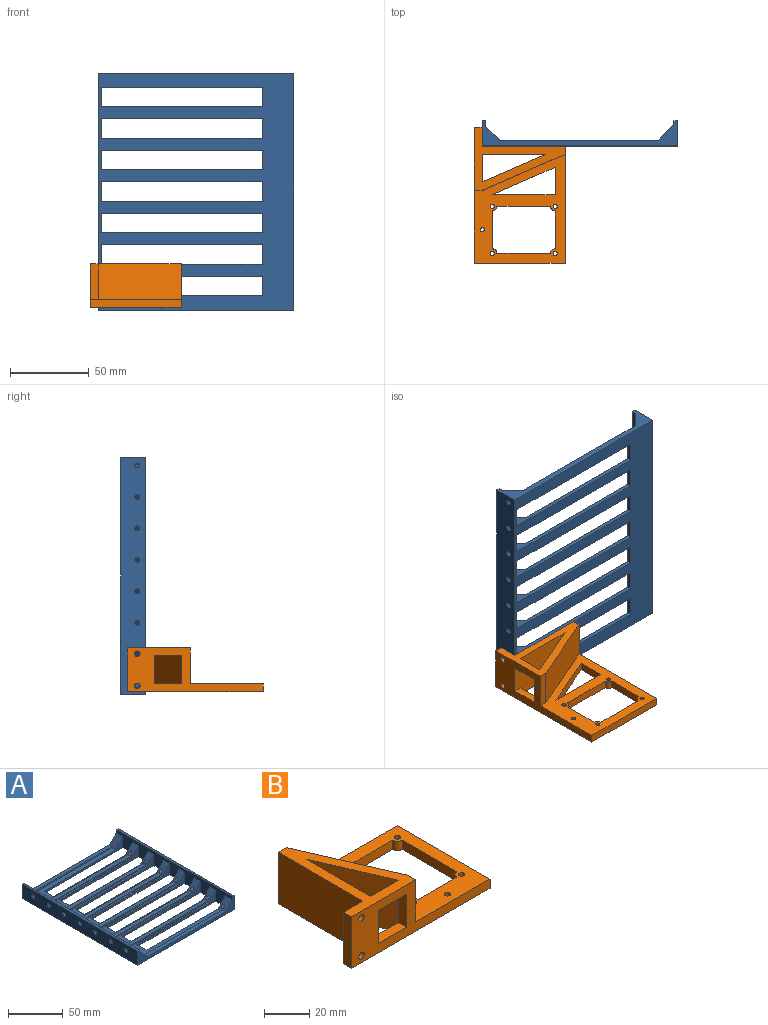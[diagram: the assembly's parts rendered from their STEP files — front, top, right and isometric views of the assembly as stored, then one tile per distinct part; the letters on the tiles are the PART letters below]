
ASSEMBLY  parts=2 mates=1
PART A: 90 faces, bbox 124.9x150.7x16.7 mm
  f0: plane 10.65x10.65mm, normal (-0.71,0,0.71), area 109.8mm2, adj f4,f6,f14,f28,f63,f64,f89
  f1: plane 10.65x10.65mm, normal (-0.71,0,0.71), area 102.7mm2, adj f4,f7,f27,f29,f77,f78,f82
  f2: plane 10.65x10.65mm, normal (-0.71,0,0.71), area 88.6mm2, adj f4,f8,f10,f21,f22,f71,f72,f73
  f3: plane 109.7x16mm, normal (0,0,1), area 605.2mm2, adj f12,f18,f19,f34,f48,f49,f59,f60
  f4: plane 150x16mm, normal (-1,0,0), area 1625mm2, adj f0,f1,f2,f9,f11,f14,f15,f16
  f5: plane 109.7x16mm, normal (0,0,1), area 605.2mm2, adj f12,f16,f17,f35,f47,f48,f57,f76
  f6: plane 109.7x19.25mm, normal (0,0,1), area 961.7mm2, adj f0,f12,f14,f15,f36,f47,f64,f74
  f7: plane 109.7x18.75mm, normal (0,0,1), area 906.9mm2, adj f1,f9,f12,f27,f30,f45,f67,f77
  f8: plane 109.7x16mm, normal (0,0,1), area 605.2mm2, adj f2,f12,f20,f21,f33,f49,f62,f71
  f9: plane 102x12.4mm, normal (0,1,0), area 294.8mm2, adj f4,f7,f11,f30,f45
  f10: plane 109.7x16mm, normal (0,0,1), area 605.2mm2, adj f2,f12,f22,f23,f32,f46,f68,f73
  f11: plane 150x124.2mm, normal (0,0,-1), area 9705mm2, adj f4,f9,f13,f14,f15,f16,f17,f18
  f12: plane 150x13.6mm, normal (1,0,0), area 1589.2mm2, adj f3,f5,f6,f7,f8,f10,f28,f29
  f13: plane 150x16mm, normal (-1,0,0), area 2307.6mm2, adj f11,f28,f29,f50,f51,f52,f53,f54
  f14: plane 102x12.4mm, normal (0,1,0), area 294.8mm2, adj f0,f4,f6,f11,f36
  f15: plane 102x12.4mm, normal (0,-1,0), area 294.8mm2, adj f4,f6,f11,f36,f47
  f16: plane 102x12.4mm, normal (0,1,0), area 294.8mm2, adj f4,f5,f11,f35,f47
  f17: plane 102x12.4mm, normal (0,-1,0), area 294.8mm2, adj f4,f5,f11,f35,f48
  f18: plane 102x12.4mm, normal (0,1,0), area 294.8mm2, adj f3,f4,f11,f34,f48
  f19: plane 102x12.4mm, normal (0,-1,0), area 294.8mm2, adj f3,f4,f11,f34,f49
  f20: plane 102x12.4mm, normal (0,1,0), area 294.8mm2, adj f4,f8,f11,f33,f49
  f21: plane 102x12.4mm, normal (0,-1,0), area 294.8mm2, adj f2,f4,f8,f11,f33
  f22: plane 102x12.4mm, normal (0,1,0), area 294.8mm2, adj f2,f4,f10,f11,f32
  f23: plane 102x12.4mm, normal (0,-1,0), area 294.8mm2, adj f4,f10,f11,f32,f46
  f24: plane 102x12.4mm, normal (0,1,0), area 294.8mm2, adj f4,f11,f31,f46,f79
  f25: plane 102x12.4mm, normal (0,-1,0), area 294.8mm2, adj f4,f11,f31,f45,f79
  f26: plane 150x16mm, normal (1,0,0), area 2339.6mm2, adj f11,f28,f29,f81,f82,f83,f84,f85
  f27: plane 102x12.4mm, normal (0,-1,0), area 294.8mm2, adj f1,f4,f7,f11,f30
  f28: plane 124.2x16mm, normal (0,-1,0), area 591.6mm2, adj f0,f4,f11,f12,f13,f26,f37,f63
  f29: plane 124.2x16mm, normal (0,1,0), area 591.6mm2, adj f1,f4,f11,f12,f13,f26,f43,f78
  f30: plane 12.5x2.4mm, normal (1,0,0), area 30mm2, adj f7,f9,f11,f27
  f31: plane 12.5x2.4mm, normal (1,0,0), area 30mm2, adj f11,f24,f25,f79
  f32: plane 12.5x2.4mm, normal (1,0,0), area 30mm2, adj f10,f11,f22,f23
  f33: plane 12.5x2.4mm, normal (1,0,0), area 30mm2, adj f8,f11,f20,f21
  f34: plane 12.5x2.4mm, normal (1,0,0), area 30mm2, adj f3,f11,f18,f19
  f35: plane 12.5x2.4mm, normal (1,0,0), area 30mm2, adj f5,f11,f16,f17
  f36: plane 12.5x2.4mm, normal (1,0,0), area 30mm2, adj f6,f11,f14,f15
  f37: plane 10x10mm, normal (0.71,0,0.71), area 56.6mm2, adj f12,f28,f63,f64
  f38: plane 10x10mm, normal (0.71,0,0.71), area 56.6mm2, adj f12,f74,f75,f76
  f39: plane 10x10mm, normal (0.71,0,0.71), area 56.6mm2, adj f12,f57,f58,f59
  f40: plane 10x10mm, normal (0.71,0,0.71), area 56.6mm2, adj f12,f60,f61,f62
  f41: plane 10x10mm, normal (0.71,0,0.71), area 56.6mm2, adj f12,f71,f72,f73
  f42: plane 10x10mm, normal (0.71,0,0.71), area 56.6mm2, adj f12,f68,f69,f70
  f43: plane 10x10mm, normal (0.71,0,0.71), area 56.6mm2, adj f12,f29,f77,f78
  f44: plane 10x10mm, normal (0.71,0,0.71), area 56.6mm2, adj f12,f65,f66,f67
  f45: plane 10.65x10.65mm, normal (-0.71,0,0.71), area 88.6mm2, adj f4,f7,f9,f25,f65,f66,f67,f79
  f46: plane 10.65x10.65mm, normal (-0.71,0,0.71), area 88.6mm2, adj f4,f10,f23,f24,f68,f69,f70,f79
  f47: plane 10.65x10.65mm, normal (-0.71,0,0.71), area 88.6mm2, adj f4,f5,f6,f15,f16,f74,f75,f76
  f48: plane 10.65x10.65mm, normal (-0.71,0,0.71), area 88.6mm2, adj f3,f4,f5,f17,f18,f57,f58,f59
  f49: plane 10.65x10.65mm, normal (-0.71,0,0.71), area 88.6mm2, adj f3,f4,f8,f19,f20,f60,f61,f62
  f50: cylinder r=2.05mm len=4.1mm, axis (-1,0,0), area 30.9mm2, adj f12,f13
  f51: cylinder r=2.05mm len=4.1mm, axis (-1,0,0), area 30.9mm2, adj f12,f13
  f52: cylinder r=2.05mm len=4.1mm, axis (-1,0,0), area 30.9mm2, adj f12,f13
  f53: cylinder r=2.05mm len=4.1mm, axis (-1,0,0), area 30.9mm2, adj f12,f13
  f54: cylinder r=2.05mm len=4.1mm, axis (-1,0,0), area 30.9mm2, adj f12,f13
  f55: cylinder r=2.05mm len=4.1mm, axis (-1,0,0), area 30.9mm2, adj f12,f13
  f56: cylinder r=2.05mm len=4.1mm, axis (-1,0,0), area 30.9mm2, adj f12,f13
  f57: plane 110.9x11.2mm, normal (0,-1,0), area 182.4mm2, adj f5,f12,f39,f48,f58
  f58: plane 100.9x4mm, normal (0,0,1), area 403.6mm2, adj f39,f48,f57,f59
  f59: plane 110.9x11.2mm, normal (0,1,0), area 182.4mm2, adj f3,f12,f39,f48,f58
  f60: plane 110.9x11.2mm, normal (0,-1,0), area 182.4mm2, adj f3,f12,f40,f49,f61
  f61: plane 100.9x4mm, normal (0,0,1), area 403.6mm2, adj f40,f49,f60,f62
  f62: plane 110.9x11.2mm, normal (0,1,0), area 182.4mm2, adj f8,f12,f40,f49,f61
  f63: plane 100.9x4mm, normal (0,0,1), area 403.6mm2, adj f0,f28,f37,f64
  f64: plane 110.9x11.2mm, normal (0,1,0), area 182.4mm2, adj f0,f6,f12,f37,f63
  f65: plane 110.9x11.2mm, normal (0,-1,0), area 182.4mm2, adj f12,f44,f45,f66,f79
  f66: plane 100.9x4mm, normal (0,0,1), area 403.6mm2, adj f44,f45,f65,f67
  f67: plane 110.9x11.2mm, normal (0,1,0), area 182.4mm2, adj f7,f12,f44,f45,f66
  f68: plane 110.9x11.2mm, normal (0,-1,0), area 182.4mm2, adj f10,f12,f42,f46,f69
  f69: plane 100.9x4mm, normal (0,0,1), area 403.6mm2, adj f42,f46,f68,f70
  f70: plane 110.9x11.2mm, normal (0,1,0), area 182.4mm2, adj f12,f42,f46,f69,f79
  f71: plane 110.9x11.2mm, normal (0,-1,0), area 182.4mm2, adj f2,f8,f12,f41,f72
  f72: plane 100.9x4mm, normal (0,0,1), area 403.6mm2, adj f2,f41,f71,f73
  f73: plane 110.9x11.2mm, normal (0,1,0), area 182.4mm2, adj f2,f10,f12,f41,f72
  f74: plane 110.9x11.2mm, normal (0,-1,0), area 182.4mm2, adj f6,f12,f38,f47,f75
  f75: plane 100.9x4mm, normal (0,0,1), area 403.6mm2, adj f38,f47,f74,f76
  f76: plane 110.9x11.2mm, normal (0,1,0), area 182.4mm2, adj f5,f12,f38,f47,f75
  f77: plane 110.9x11.2mm, normal (0,-1,0), area 182.4mm2, adj f1,f7,f12,f43,f78
  f78: plane 100.9x4mm, normal (0,0,1), area 403.6mm2, adj f1,f29,f43,f77
  f79: plane 109.7x16mm, normal (0,0,1), area 605.2mm2, adj f12,f24,f25,f31,f45,f46,f65,f70
  f80: plane 150x2.4mm, normal (0,0,1), area 360mm2, adj f12,f13,f28,f29
  f81: plane 150x2.1mm, normal (0,0,1), area 315mm2, adj f4,f26,f28,f29
  f82: cylinder r=1.55mm len=10.55mm, axis (1,0,0), area 87.1mm2, adj f1,f26
  f83: cylinder r=1.55mm len=10.55mm, axis (1,0,0), area 87.1mm2, adj f26,f45
  f84: cylinder r=1.55mm len=10.55mm, axis (1,0,0), area 87.1mm2, adj f26,f46
  f85: cylinder r=1.55mm len=10.55mm, axis (1,0,0), area 87.1mm2, adj f2,f26
  f86: cylinder r=1.55mm len=10.55mm, axis (1,0,0), area 87.1mm2, adj f26,f49
  f87: cylinder r=1.55mm len=10.55mm, axis (1,0,0), area 87.1mm2, adj f26,f48
  f88: cylinder r=1.55mm len=10.55mm, axis (1,0,0), area 87.1mm2, adj f26,f47
  f89: cylinder r=1.55mm len=10.55mm, axis (1,0,0), area 87.1mm2, adj f0,f26
PART B: 36 faces, bbox 86.4x57.7x27.8 mm
  f0: plane 17.5x5mm, normal (0,1,0), area 87.5mm2, adj f5,f6,f20,f33
  f1: plane 86.35x27.77mm, normal (0,-1,0), area 1012.4mm2, adj f2,f3,f5,f6,f7,f8,f9,f10
  f2: plane 86.35x57.7mm, normal (0,0,-1), area 2447.1mm2, adj f1,f4,f5,f7,f11,f12,f13,f14
  f3: plane 69.3x57.7mm, normal (0,0,1), area 1730.4mm2, adj f1,f10,f13,f14,f15,f16,f17,f18
  f4: plane 17.5x5mm, normal (0,1,0), area 87.5mm2, adj f2,f5,f20,f35
  f5: plane 45.18x27.77mm, normal (1,0,0), area 1204.6mm2, adj f0,f1,f2,f4,f6,f20,f33,f35
  f6: plane 57.7x40mm, normal (0,0,1), area 716.8mm2, adj f0,f1,f5,f7,f10,f11,f12,f13
  f7: plane 27.77x5mm, normal (-1,0,0), area 138.8mm2, adj f1,f2,f6,f11
  f8: cylinder r=1.75mm len=5mm, axis (0,-1,0), area 55mm2, adj f1,f11
  f9: cylinder r=1.75mm len=5mm, axis (0,-1,0), area 55mm2, adj f1,f11
  f10: plane 22.77x5mm, normal (1,0,0), area 113.8mm2, adj f1,f3,f6,f19
  f11: plane 27.77x12.05mm, normal (0,1,0), area 315.4mm2, adj f2,f6,f7,f8,f9,f12
  f12: plane 52.7x27.77mm, normal (-1,0,0), area 1463.5mm2, adj f2,f6,f11,f13
  f13: plane 74.3x27.77mm, normal (0,1,0), area 485.3mm2, adj f2,f3,f6,f12,f14,f19
  f14: plane 57.7x5mm, normal (1,0,0), area 288.5mm2, adj f1,f2,f3,f13
  f15: cylinder r=1.35mm len=5mm, axis (0,0,-1), area 42.4mm2, adj f2,f3
  f16: cylinder r=1.35mm len=5mm, axis (0,0,-1), area 42.4mm2, adj f2,f3
  f17: cylinder r=1.35mm len=5mm, axis (0,0,-1), area 42.4mm2, adj f2,f3
  f18: cylinder r=1.35mm len=5mm, axis (0,0,-1), area 42.4mm2, adj f2,f3
  f19: plane 52.7x22.95mm, normal (0.92,0.4,0), area 1308.8mm2, adj f3,f6,f10,f13
  f20: plane 40.18x27.77mm, normal (-0.92,-0.4,0), area 1216.9mm2, adj f0,f2,f4,f5,f6,f34
  f21: plane 40x5mm, normal (-1,0,0), area 200mm2, adj f2,f3,f22,f23
  f22: plane 17.42x5mm, normal (0,-1,0), area 87.1mm2, adj f2,f3,f21,f23
  f23: plane 40x17.42mm, normal (0.92,0.4,0), area 218.1mm2, adj f2,f3,f21,f22
  f24: plane 24x5mm, normal (0,1,0), area 120mm2, adj f2,f3,f28,f29
  f25: plane 34x5mm, normal (-1,0,0), area 170mm2, adj f2,f3,f29,f30
  f26: plane 24x5mm, normal (0,-1,0), area 120mm2, adj f2,f3,f30,f31
  f27: plane 34x5mm, normal (1,0,0), area 170mm2, adj f2,f3,f28,f31
  f28: cylinder r=3mm len=5mm, axis (0,0,1), area 23.6mm2, adj f2,f3,f24,f27
  f29: cylinder r=3mm len=5mm, axis (0,0,1), area 23.6mm2, adj f2,f3,f24,f25
  f30: cylinder r=3mm len=5mm, axis (0,0,1), area 23.6mm2, adj f2,f3,f25,f26
  f31: cylinder r=3mm len=5mm, axis (0,0,1), area 23.6mm2, adj f2,f3,f26,f27
  f32: cylinder r=1.35mm len=5mm, axis (0,0,1), area 42.4mm2, adj f2,f3
  f33: plane 17.5x5mm, normal (0,0,-1), area 87.5mm2, adj f0,f1,f5,f34
  f34: plane 17.77x5mm, normal (-1,0,0), area 88.8mm2, adj f1,f20,f33,f35
  f35: plane 17.5x5mm, normal (0,0,1), area 87.5mm2, adj f1,f4,f5,f34
PLACE A rot(axis=(0,-0.71,-0.71),180deg) t=(-145.3,31.3,-50.12)mm
PLACE B rot(axis=(0,0,-1),90deg) t=(-212.4,23.15,-109.69)mm
MATE fastened B.f9 <-> A.f89  axis (1,0,0) through (-207.4,36.8,-119.87)mm
